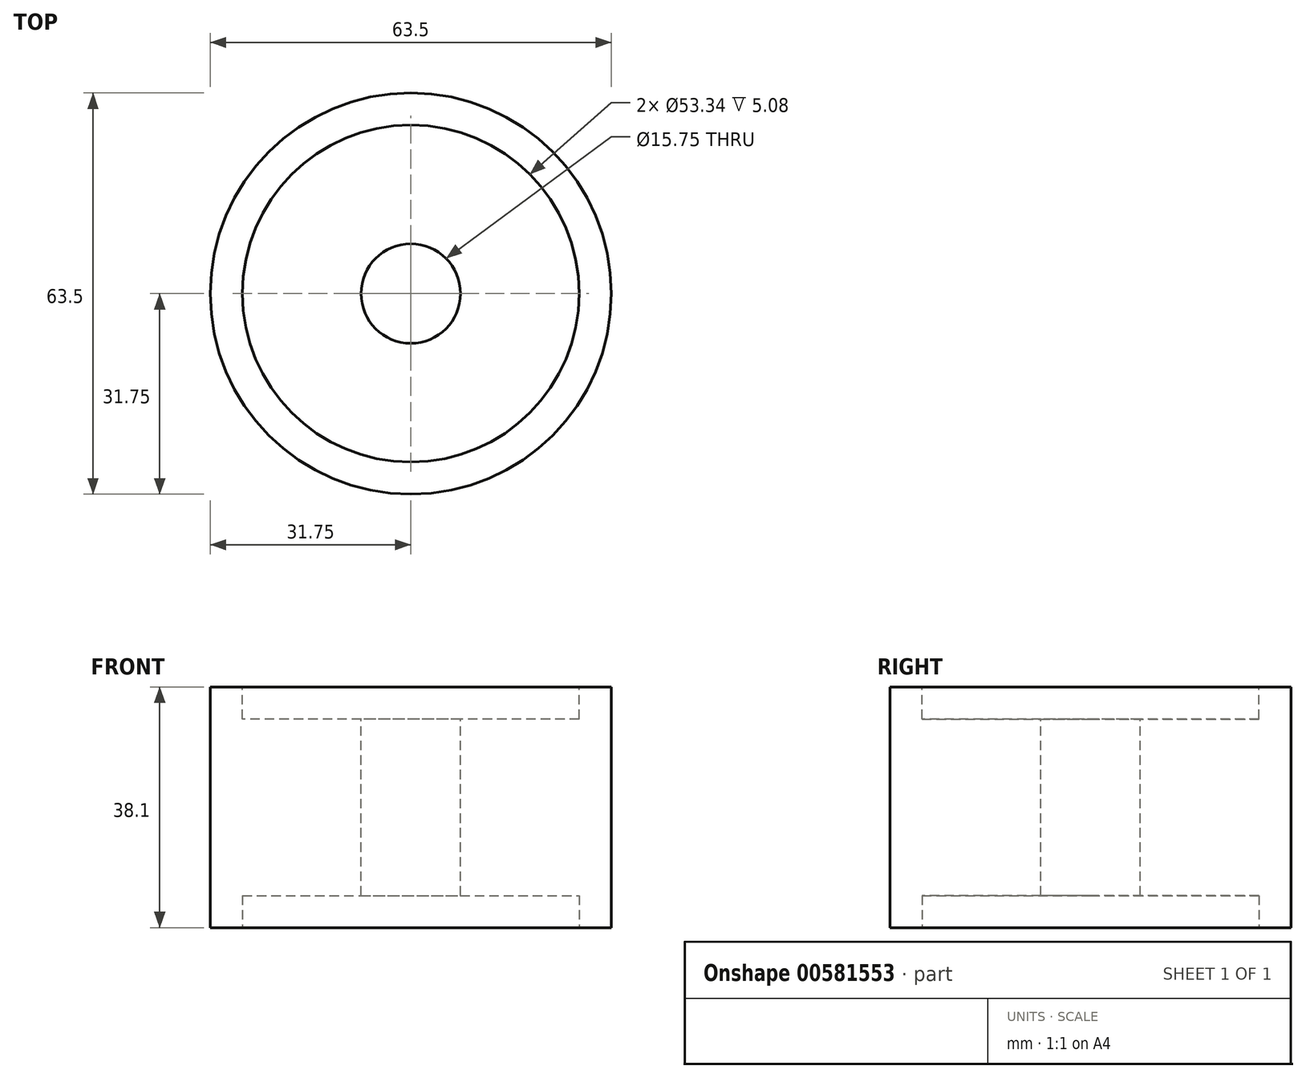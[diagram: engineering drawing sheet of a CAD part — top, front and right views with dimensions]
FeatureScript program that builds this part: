
annotation { "Feature Type Name" : "Feature", "Feature Type Description" : "" }
export const myFeature = defineFeature(function(context is Context, id is Id, definition is map)
    precondition{}
    {
        {
            var Q0;
            Q0=qCreatedBy(makeId("Top.planeOp"),FACE);
            var sketch = newSketch(context, id + "F0", { "sketchPlane" : qUnion([Q0])});
            skCircle(sketch, "E0", {"center": v(0, 0) * mm, "radius": 31.75 * mm});
            skSolve(sketch);
        }
        {
            var Q0;
            Q0=makeQuery(id+"F0.imprint","IMPRINT",FACE,{"disambiguationData":[TD([[makeQuery(id+"F0.imprint","IMPRINT",EDGE,{"derivedFrom":sQuery(id+"F0.wireOp",EDGE,"E0")}),1.0]])]});
            extrude(context, id + "F1", {"entities" : qUnion([Q0]), "depth" : 38.1 * mm, "offsetDistance" : 25.4 * mm, "symmetric" : true});
        }
        {
            var Q0;
            Q0=makeQuery(id+"F1.opExtrude","CAP_FACE",FACE,{"disambiguationData":[OSD([sQuery(id+"F0.wireOp",EDGE,"E0")])],"isStart":false});
            var sketch = newSketch(context, id + "F2", { "sketchPlane" : qUnion([Q0])});
            skCircle(sketch, "E1", {"center": v(0, 0) * mm, "radius": 26.67 * mm});
            skSolve(sketch);
        }
        {
            var Q0;
            Q0=makeQuery(id+"F1.opExtrude","CAP_FACE",FACE,{"disambiguationData":[OSD([sQuery(id+"F0.wireOp",EDGE,"E0")])],"isStart":true});
            var sketch = newSketch(context, id + "F3", { "sketchPlane" : qUnion([Q0])});
            skCircle(sketch, "E2", {"center": v(0, 0) * mm, "radius": 26.67 * mm});
            skSolve(sketch);
        }
        {
            var Q0;
            Q0=makeQuery(id+"F2.imprint","IMPRINT",FACE,{"disambiguationData":[TD([[makeQuery(id+"F2.imprint","IMPRINT",EDGE,{"derivedFrom":sQuery(id+"F2.wireOp",EDGE,"E1")}),1.0]])]});
            extrude(context, id + "F4", {"entities" : qUnion([Q0]), "operationType" : NewBodyOperationType.REMOVE, "oppositeDirection" : true, "depth" : 5.08 * mm, "offsetDistance" : 25.4 * mm});
        }
        {
            var Q0;
            Q0=makeQuery(id+"F3.imprint","IMPRINT",FACE,{"disambiguationData":[TD([[makeQuery(id+"F3.imprint","IMPRINT",EDGE,{"derivedFrom":sQuery(id+"F3.wireOp",EDGE,"E2")}),1.0]])]});
            extrude(context, id + "F5", {"entities" : qUnion([Q0]), "operationType" : NewBodyOperationType.REMOVE, "oppositeDirection" : true, "depth" : 5.08 * mm, "offsetDistance" : 25.4 * mm});
        }
        {
            var Q0;
            Q0=makeQuery(id+"F4.boolean.opBoolean","COPY",FACE,{"derivedFrom":makeQuery(id+"F4.opExtrude","CAP_FACE",FACE,{"disambiguationData":[OSD([sQuery(id+"F2.wireOp",EDGE,"E1")])],"isStart":false})});
            var sketch = newSketch(context, id + "F6", { "sketchPlane" : qUnion([Q0])});
            skCircle(sketch, "E3", {"center": v(0, 0) * mm, "radius": 7.87 * mm});
            skSolve(sketch);
        }
        {
            var Q0;
            Q0=makeQuery(id+"F6.imprint","IMPRINT",FACE,{"disambiguationData":[TD([[makeQuery(id+"F6.imprint","IMPRINT",EDGE,{"derivedFrom":sQuery(id+"F6.wireOp",EDGE,"E3")}),1.0]])]});
            extrude(context, id + "F7", {"entities" : qUnion([Q0]), "operationType" : NewBodyOperationType.REMOVE, "oppositeDirection" : true, "depth" : 50.8 * mm, "offsetDistance" : 25.4 * mm});
        }
    });
